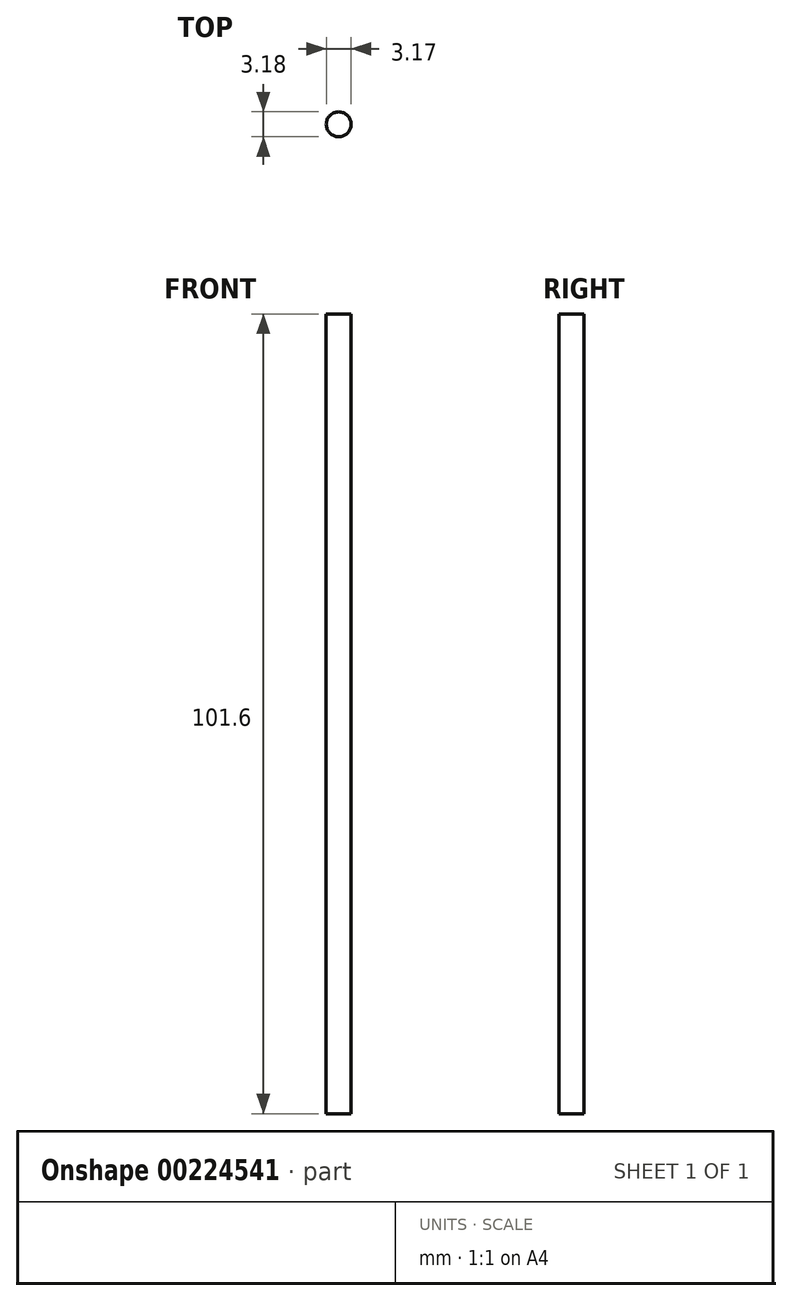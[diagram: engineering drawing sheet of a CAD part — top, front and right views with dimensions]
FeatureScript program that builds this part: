
annotation { "Feature Type Name" : "Feature", "Feature Type Description" : "" }
export const myFeature = defineFeature(function(context is Context, id is Id, definition is map)
    precondition{}
    {
        {
            var Q0;
            Q0=qCreatedBy(makeId("Top.planeOp"),FACE);
            var sketch = newSketch(context, id + "F0", { "sketchPlane" : qUnion([Q0])});
            skCircle(sketch, "E0", {"center": v(-132.07, -24.71) * mm, "radius": 1.59 * mm});
            skSolve(sketch);
        }
        {
            var Q0;
            Q0 = qSketchRegion(id + "F0", true);
            extrude(context, id + "F1", {"entities" : qUnion([Q0]), "depth" : 101.6 * mm});
        }
    });
